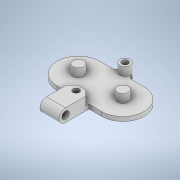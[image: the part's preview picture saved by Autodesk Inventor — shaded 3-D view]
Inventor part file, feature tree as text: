
AUTODESK INVENTOR PART (.ipt)
format: ipt  version: 2021 (Build 250183000, 183)  size: 175,104 bytes
history: native  units: mm
features: extrude x3, sketch x2, other x1, projected_geometry x1
ambient origin geometry x8: Origin, YZ Plane, XZ Plane, XY Plane, X Axis, Y Axis, Z Axis, Center Point
bodies: Body1 (feature_tree)
feature tree (7):
  other  "Sólido1"
  sketch  "Boceto1"  dims[d10=5.0mm d11=20.0mm]
  extrude  "Extrusión1"  Depth=20.0mm
  extrude  "Extrusión2"  Depth=20.0mm
  extrude  "Extrusión3"  Depth=9.0mm
  sketch  "Boceto2"  dims[d13=5.0mm d14=20.0mm d19=9.0mm d20=14.0mm d25=3.0mm d27=3.0mm d28=5.0mm d29=2.5mm d30=5.0mm d31=6.0mm d32=0.0mm d33=2.0mm d34=0.0mm d35=3.0mm d36=3.0mm d37=6.0mm d38=3.5mm d39=9.0mm d40=0.0mm]
  projected_geometry  "Contorno proyectado1"
